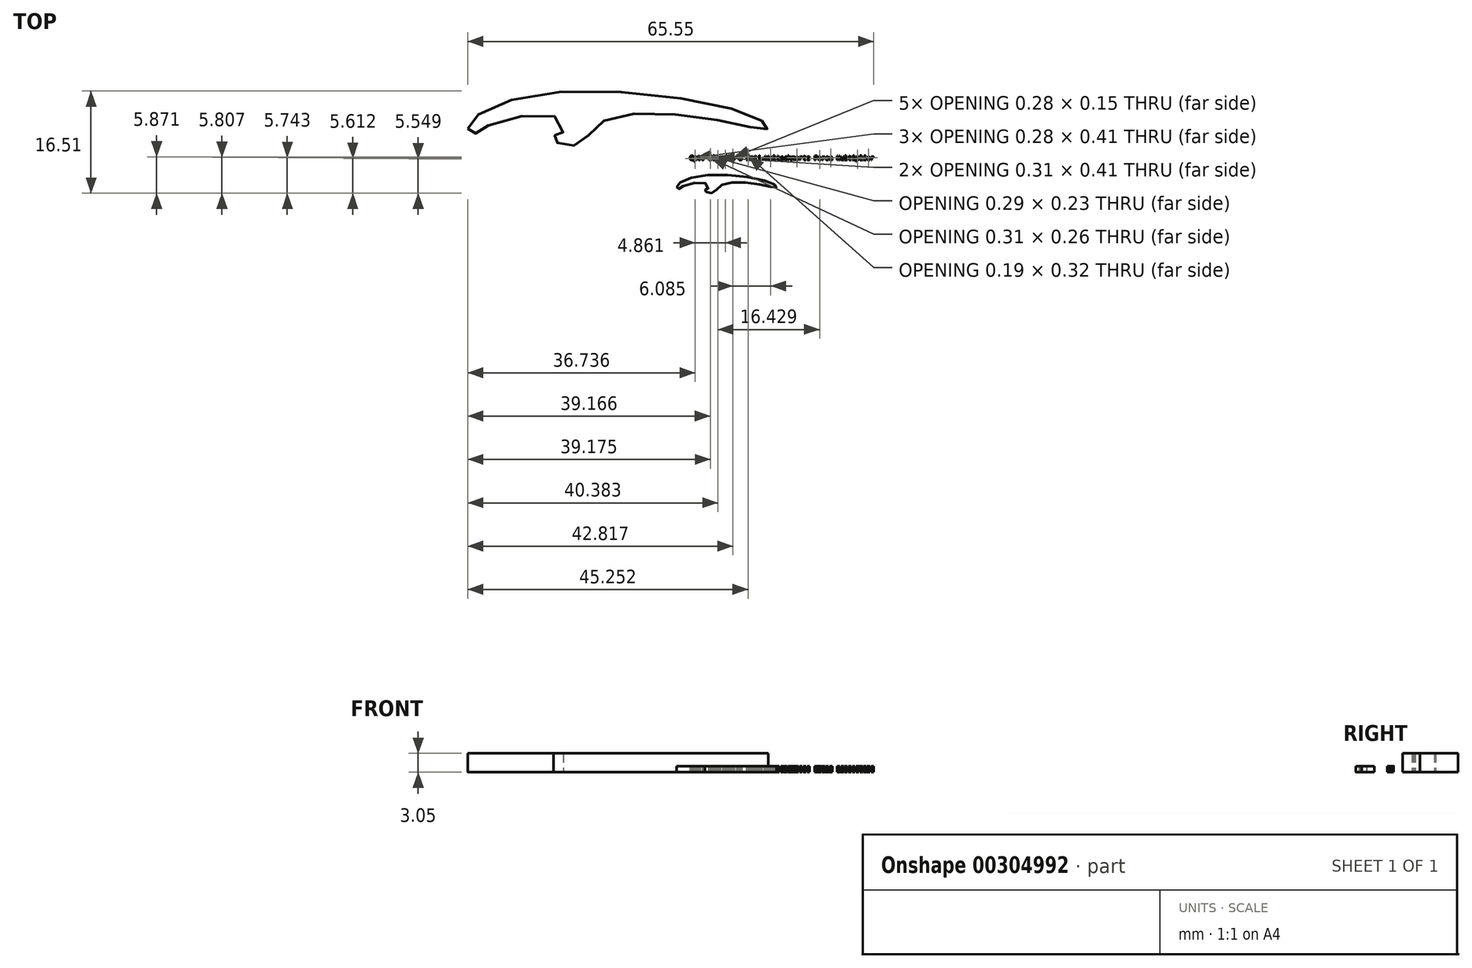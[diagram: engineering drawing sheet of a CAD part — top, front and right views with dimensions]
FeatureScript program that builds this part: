
annotation { "Feature Type Name" : "Feature", "Feature Type Description" : "" }
export const myFeature = defineFeature(function(context is Context, id is Id, definition is map)
    precondition{}
    {
        {
            var Q0;
            Q0=qCreatedBy(makeId("Top.planeOp"),FACE);
            var sketch = newSketch(context, id + "F0", { "sketchPlane" : qUnion([Q0])});
            skFitSpline(sketch, "E0", {"points": [v(-16.84, 4.74) * mm, v(-13.36, 6.54) * mm, v(-1.26, 5.3) * mm, v(-0.7, 4.74) * mm, v(-2.96, 5.11) * mm, v(-9.44, 5.2) * mm, v(-10.79, 3.96) * mm, v(-12.02, 3.96) * mm, v(-12.22, 4.37) * mm, v(-11.88, 4.3) * mm, v(-11.94, 5.27) * mm, v(-16.12, 4.72) * mm, v(-16.48, 4.47) * mm, v(-16.84, 4.74) * mm]});
            skText(sketch, "E1", { "text": "Cpt. Blondie\'s Anti-Weltschmertz Force Multiplier", "fontName": "DroidSansMono.ttf"});
            const initialGuessF0  = {"E1": [-0.01472, 0.00912, 1, 0, 0.00073]};
            skSetInitialGuess(sketch, initialGuessF0);
            skSolve(sketch);
        }
        {
            var Q0;
            Q0=makeQuery(id+"F0.imprint","IMPRINT",FACE,{"disambiguationData":[TD([[makeQuery(id+"F0.imprint","IMPRINT",EDGE,{"derivedFrom":sQuery(id+"F0.wireOp",EDGE,"E0")}),-1.0]])]});
            extrude(context, id + "F1", {"entities" : qUnion([Q0]), "depth" : 1.02 * mm});
        }
        {
            var Q0;
            Q0=makeQuery(id+"F1.opExtrude","SWEPT_BODY",BODY,{"disambiguationData":[OSD([sQuery(id+"F0.wireOp",EDGE,"E0")])]});
            var Q1;
            Q1=qCreatedBy(makeId("Origin.pointOp"),VERTEX);
            transform(context, id + "F2", {"entities" : qUnion([Q0]), "transformType" : TransformType.SCALE_UNIFORMLY, "scale" : 3, "scalePoint" : qUnion([Q1]), "makeCopy" : false});
        }
        {
            var Q0;
            Q0 = qSketchRegion(id + "F0", true);
            extrude(context, id + "F3", {"entities" : qUnion([Q0]), "depth" : 1 * mm});
        }
    });
